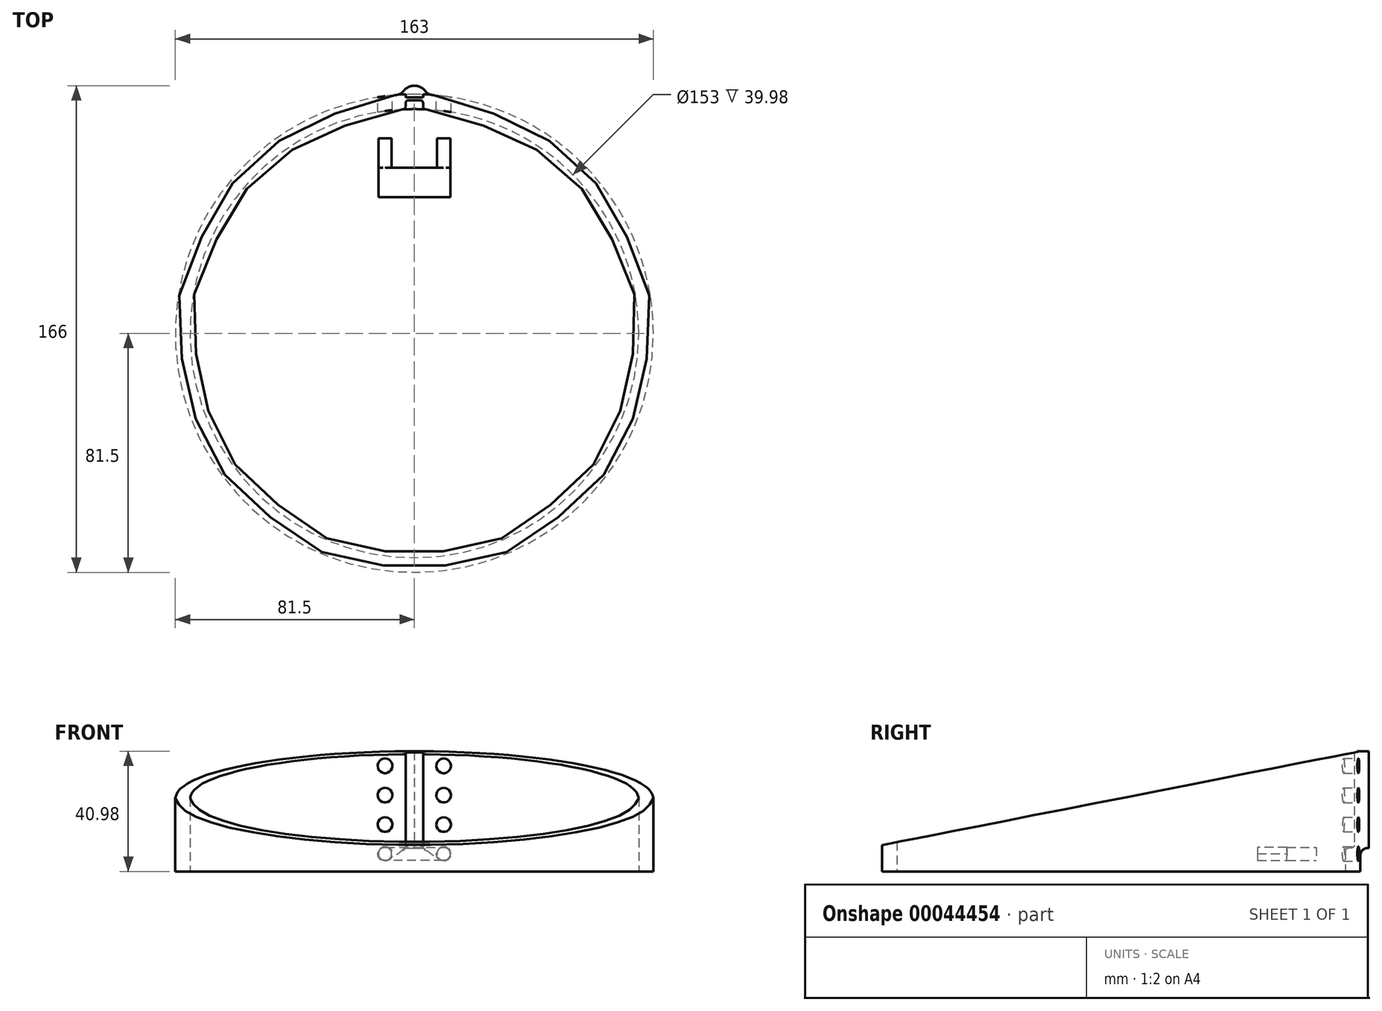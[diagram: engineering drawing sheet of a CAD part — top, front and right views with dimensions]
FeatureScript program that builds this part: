
annotation { "Feature Type Name" : "Feature", "Feature Type Description" : "" }
export const myFeature = defineFeature(function(context is Context, id is Id, definition is map)
    precondition{}
    {
        {
            var Q0;
            Q0=qCreatedBy(makeId("Top.planeOp"),FACE);
            var sketch = newSketch(context, id + "F0", { "sketchPlane" : qUnion([Q0])});
            skCircle(sketch, "E0", {"center": v(0, 0) * mm, "radius": 76.5 * mm});
            skCircle(sketch, "E1.0", {"center": v(0, 0) * mm, "radius": 81.5 * mm});
            skSolve(sketch);
        }
        {
            var Q0;
            Q0=qCreatedBy(makeId("Right.planeOp"),FACE);
            var sketch = newSketch(context, id + "F1", { "sketchPlane" : qUnion([Q0])});
            skLineSegment(sketch, "E2.0.0", {"start": v(-76.5, 0) * mm, "end": v(76.5, 0) * mm});
            skLineSegment(sketch, "E3", {"start": v(-76.5, 0) * mm, "end": v(-76.5, 10) * mm});
            skLineSegment(sketch, "E4", {"start": v(76.5, 0) * mm, "end": v(76.5, 40) * mm});
            skSolve(sketch);
        }
        {
            var Q0;
            Q0=sQuery(id+"F1.wireOp",VERTEX,"E3.end");
            var Q1;
            Q1=qCreatedBy(makeId("Front.planeOp"),FACE);
            cPlane(context, id + "F2", {"entities" : qUnion([Q0, Q1]), "cplaneType" : CPlaneType.PLANE_POINT, "offset" : 150 * mm, "width" : 150 * mm, "height" : 150 * mm});
        }
        {
            var Q0;
            Q0=qCreatedBy(id+"F2.planeOp",FACE);
            var sketch = newSketch(context, id + "F3", { "sketchPlane" : qUnion([Q0])});
            skLineSegment(sketch, "E5", {"start": v(0, 10) * mm, "end": v(-21.8, 10) * mm});
            skSolve(sketch);
        }
        {
            var Q0;
            Q0=sQuery(id+"F3.wireOp",EDGE,"E5");
            var Q1;
            Q1=sQuery(id+"F1.wireOp",VERTEX,"E4.end");
            cPlane(context, id + "F4", {"entities" : qUnion([Q0, Q1]), "cplaneType" : CPlaneType.LINE_ANGLE, "offset" : 150 * mm, "angle" : 0 * degree, "width" : 150 * mm, "height" : 150 * mm});
        }
        {
            var Q0;
            Q0=sQuery(id+"F1.wireOp",VERTEX,"E4.end");
            var Q1;
            Q1=qCreatedBy(makeId("Top.planeOp"),FACE);
            cPlane(context, id + "F5", {"entities" : qUnion([Q0, Q1]), "cplaneType" : CPlaneType.PLANE_POINT, "offset" : 150 * mm, "width" : 150 * mm, "height" : 150 * mm});
        }
        {
            var Q0;
            Q0=makeQuery(id+"F0.imprint","IMPRINT",FACE,{"disambiguationData":[TD([[makeQuery(id+"F0.imprint","IMPRINT",EDGE,{"derivedFrom":sQuery(id+"F0.wireOp",EDGE,"E0")}),-1.0]])]});
            var Q1;
            Q1=sQuery(id+"F0.wireOp",EDGE,"E1.0");
            var Q2;
            Q2=qCreatedBy(id+"F4.planeOp",FACE);
            extrude(context, id + "F6", {"entities" : qUnion([Q0]), "surfaceEntities" : qUnion([Q1]), "endBound" : BoundingType.UP_TO_SURFACE, "endBoundEntityFace" : qUnion([Q2]), "depth" : 19.21 * mm});
        }
        {
            var Q0;
            Q0=makeQuery(id+"F6.opExtrude","CAP_FACE",FACE,{"disambiguationData":[OSD([sQuery(id+"F0.wireOp",EDGE,"E0"),sQuery(id+"F0.wireOp",EDGE,"E1.0")])],"isStart":false});
            var sketch = newSketch(context, id + "F7", { "sketchPlane" : qUnion([Q0])});
            skLineSegment(sketch, "E6", {"start": v(-35.1, 87.86) * mm, "end": v(35.1, 87.86) * mm});
            skPoint(sketch, "E6.startSnap0", {"position": v(0, 87.86) * mm});
            skSolve(sketch);
        }
        {
            var Q0;
            Q0=sQuery(id+"F7.wireOp",EDGE,"E6");
            var Q1;
            Q1=qCreatedBy(makeId("Front.planeOp"),FACE);
            cPlane(context, id + "F8", {"entities" : qUnion([Q0, Q1]), "cplaneType" : CPlaneType.LINE_ANGLE, "offset" : 150 * mm, "angle" : 0 * degree, "width" : 150 * mm, "height" : 150 * mm});
        }
        {
            var Q0;
            Q0=qCreatedBy(id+"F8.planeOp",FACE);
            var sketch = newSketch(context, id + "F9", { "sketchPlane" : qUnion([Q0])});
            skLineSegment(sketch, "E7.0", {"start": v(35.1, 40.98) * mm, "end": v(-35.1, 40.98) * mm});
            skCircle(sketch, "E8", {"center": v(10, 36) * mm, "radius": 2.5 * mm});
            skCircle(sketch, "E9.0.1.0", {"center": v(-10, 36) * mm, "radius": 2.5 * mm});
            skCircle(sketch, "E9.1.0.0", {"center": v(10, 26) * mm, "radius": 2.5 * mm});
            skCircle(sketch, "E9.1.1.0", {"center": v(-10, 26) * mm, "radius": 2.5 * mm});
            skCircle(sketch, "E9.2.0.0", {"center": v(10, 16) * mm, "radius": 2.5 * mm});
            skCircle(sketch, "E9.2.1.0", {"center": v(-10, 16) * mm, "radius": 2.5 * mm});
            skLineSegment(sketch, "E9.direction1", {"start": v(10, 36) * mm, "end": v(10, 26) * mm, "construction": true});
            skLineSegment(sketch, "E9.direction2", {"start": v(10, 36) * mm, "end": v(-10, 36) * mm, "construction": true});
            skCircle(sketch, "E10.0.3.0", {"center": v(10, 6) * mm, "radius": 2.5 * mm});
            skCircle(sketch, "E10.0.3.1", {"center": v(-10, 6) * mm, "radius": 2.5 * mm});
            skSolve(sketch);
        }
        {
            var Q0;
            Q0=makeQuery(id+"F9.imprint","IMPRINT",FACE,{"disambiguationData":[TD([[makeQuery(id+"F9.imprint","IMPRINT",EDGE,{"derivedFrom":sQuery(id+"F9.wireOp",EDGE,"E9.0.1.0")}),1.0]])]});
            var Q1;
            Q1=makeQuery(id+"F9.imprint","IMPRINT",FACE,{"disambiguationData":[TD([[makeQuery(id+"F9.imprint","IMPRINT",EDGE,{"derivedFrom":sQuery(id+"F9.wireOp",EDGE,"E8")}),1.0]])]});
            var Q2;
            Q2=makeQuery(id+"F9.imprint","IMPRINT",FACE,{"disambiguationData":[TD([[makeQuery(id+"F9.imprint","IMPRINT",EDGE,{"derivedFrom":sQuery(id+"F9.wireOp",EDGE,"E9.1.0.0")}),1.0]])]});
            var Q3;
            Q3=makeQuery(id+"F9.imprint","IMPRINT",FACE,{"disambiguationData":[TD([[makeQuery(id+"F9.imprint","IMPRINT",EDGE,{"derivedFrom":sQuery(id+"F9.wireOp",EDGE,"E9.1.1.0")}),1.0]])]});
            var Q4;
            Q4=makeQuery(id+"F9.imprint","IMPRINT",FACE,{"disambiguationData":[TD([[makeQuery(id+"F9.imprint","IMPRINT",EDGE,{"derivedFrom":sQuery(id+"F9.wireOp",EDGE,"E9.2.1.0")}),1.0]])]});
            var Q5;
            Q5=makeQuery(id+"F9.imprint","IMPRINT",FACE,{"disambiguationData":[TD([[makeQuery(id+"F9.imprint","IMPRINT",EDGE,{"derivedFrom":sQuery(id+"F9.wireOp",EDGE,"E9.2.0.0")}),1.0]])]});
            var Q6;
            Q6=makeQuery(id+"F9.imprint","IMPRINT",FACE,{"disambiguationData":[TD([[makeQuery(id+"F9.imprint","IMPRINT",EDGE,{"derivedFrom":sQuery(id+"F9.wireOp",EDGE,"E10.0.3.0")}),1.0]])]});
            var Q7;
            Q7=makeQuery(id+"F9.imprint","IMPRINT",FACE,{"disambiguationData":[TD([[makeQuery(id+"F9.imprint","IMPRINT",EDGE,{"derivedFrom":sQuery(id+"F9.wireOp",EDGE,"E10.0.3.1")}),1.0]])]});
            var Q8;
            Q8=sQuery(id+"F9.wireOp",EDGE,"E8");
            var Q9;
            Q9=sQuery(id+"F9.wireOp",EDGE,"E9.0.1.0");
            var Q10;
            Q10=sQuery(id+"F9.wireOp",EDGE,"E9.1.1.0");
            var Q11;
            Q11=sQuery(id+"F9.wireOp",EDGE,"E9.1.0.0");
            var Q12;
            Q12=sQuery(id+"F9.wireOp",EDGE,"E9.2.0.0");
            var Q13;
            Q13=sQuery(id+"F9.wireOp",EDGE,"E10.0.3.0");
            var Q14;
            Q14=sQuery(id+"F9.wireOp",EDGE,"E10.0.3.1");
            var Q15;
            Q15=sQuery(id+"F9.wireOp",EDGE,"E9.2.1.0");
            var Q16;
            Q16=makeQuery(id+"F6.opExtrude","SWEPT_FACE",FACE,{"disambiguationData":[OSD([sQuery(id+"F0.wireOp",EDGE,"E0")])]});
            extrude(context, id + "F10", {"entities" : qUnion([Q0, Q1, Q2, Q3, Q4, Q5, Q6, Q7]), "operationType" : NewBodyOperationType.REMOVE, "surfaceEntities" : qUnion([Q8, Q9, Q10, Q11, Q12, Q13, Q14, Q15]), "endBound" : BoundingType.UP_TO_SURFACE, "oppositeDirection" : true, "endBoundEntityFace" : qUnion([Q16]), "depth" : 25 * mm});
        }
        {
            var Q0;
            Q0=qCreatedBy(id+"F8.planeOp",FACE);
            cPlane(context, id + "F11", {"entities" : qUnion([Q0]), "cplaneType" : CPlaneType.OFFSET, "offset" : 15 * mm, "oppositeDirection" : true, "width" : 150 * mm, "height" : 150 * mm});
        }
        {
            var Q0;
            Q0=qCreatedBy(id+"F11.planeOp",FACE);
            var sketch = newSketch(context, id + "F12", { "sketchPlane" : qUnion([Q0])});
            skCircle(sketch, "E11.0", {"center": v(10, 6) * mm, "radius": 2.5 * mm});
            skCircle(sketch, "E12.0", {"center": v(-10, 6) * mm, "radius": 2.5 * mm});
            skCircle(sketch, "E13.0", {"center": v(10, 6) * mm, "radius": 2.25 * mm});
            skCircle(sketch, "E14.0", {"center": v(-10, 6) * mm, "radius": 2.25 * mm});
            skSolve(sketch);
        }
        {
            var Q0;
            Q0=makeQuery(id+"F12.imprint","IMPRINT",FACE,{"disambiguationData":[TD([[makeQuery(id+"F12.imprint","IMPRINT",EDGE,{"derivedFrom":sQuery(id+"F12.wireOp",EDGE,"E13.0")}),1.0]])]});
            var Q1;
            Q1=makeQuery(id+"F12.imprint","IMPRINT",FACE,{"disambiguationData":[TD([[makeQuery(id+"F12.imprint","IMPRINT",EDGE,{"derivedFrom":sQuery(id+"F12.wireOp",EDGE,"E14.0")}),1.0]])]});
            var Q2;
            Q2=sQuery(id+"F12.wireOp",EDGE,"E13.0");
            var Q3;
            Q3=sQuery(id+"F12.wireOp",EDGE,"E14.0");
            extrude(context, id + "F13", {"entities" : qUnion([Q0, Q1]), "surfaceEntities" : qUnion([Q2, Q3]), "oppositeDirection" : true, "depth" : 10 * mm});
        }
        {
            var Q0;
            Q0=makeQuery(id+"F13.opExtrude","CAP_FACE",FACE,{"disambiguationData":[OSD([sQuery(id+"F12.wireOp",EDGE,"E13.0")])],"isStart":false});
            cPlane(context, id + "F14", {"entities" : qUnion([Q0]), "cplaneType" : CPlaneType.OFFSET, "offset" : 0 * mm, "width" : 150 * mm, "height" : 150 * mm});
        }
        {
            var Q0;
            Q0=qCreatedBy(id+"F14.planeOp",FACE);
            var sketch = newSketch(context, id + "F15", { "sketchPlane" : qUnion([Q0])});
            skPoint(sketch, "E15", {"position": v(0, 8.25) * mm});
            skCircle(sketch, "E16.0", {"center": v(-10, 6) * mm, "radius": 2.25 * mm});
            skCircle(sketch, "E17.0", {"center": v(10, 6) * mm, "radius": 2.25 * mm});
            skLineSegment(sketch, "E18", {"start": v(-12.25, 8.25) * mm, "end": v(12.25, 8.25) * mm});
            skLineSegment(sketch, "E19", {"start": v(12.25, 8.25) * mm, "end": v(12.25, 3.75) * mm});
            skLineSegment(sketch, "E20", {"start": v(12.25, 3.75) * mm, "end": v(-12.25, 3.75) * mm});
            skLineSegment(sketch, "E21", {"start": v(-12.25, 3.75) * mm, "end": v(-12.25, 8.25) * mm});
            skSolve(sketch);
        }
        {
            var Q0;
            {var subQ0=sQuery(id+"F15.wireOp",EDGE,"E21");var subQ1=sQuery(id+"F15.wireOp",EDGE,"E16.0");var subQ2=makeQuery(id+"F15.imprint","INTERSECT",VERTEX,{"derivedFrom":[subQ1,subQ0]});Q0=makeQuery(id+"F15.imprint","IMPRINT",FACE,{"disambiguationData":[TD([[makeQuery(id+"F15.imprint","IMPRINT",EDGE,{"disambiguationData":[TD([[subQ2,-1.0]])],"derivedFrom":subQ1}),-1.0]])]});}
            var Q1;
            {var subQ1=sQuery(id+"F15.wireOp",EDGE,"E16.0");var subQ3=sQuery(id+"F15.wireOp",EDGE,"E21");var subQ5=makeQuery(id+"F15.imprint","INTERSECT",VERTEX,{"derivedFrom":[subQ1,subQ3]});Q1=makeQuery(id+"F15.imprint","IMPRINT",FACE,{"disambiguationData":[TD([[makeQuery(id+"F15.imprint","IMPRINT",EDGE,{"disambiguationData":[TD([[subQ5,1.0]])],"derivedFrom":subQ1}),-1.0]])]});}
            var Q2;
            {var subQ0=sQuery(id+"F15.wireOp",EDGE,"E16.0");var subQ3=makeQuery(id+"F15.imprint","INTERSECT",VERTEX,{"derivedFrom":[subQ0,sQuery(id+"F15.wireOp",EDGE,"E21")]});Q2=makeQuery(id+"F15.imprint","IMPRINT",FACE,{"disambiguationData":[TD([[makeQuery(id+"F15.imprint","IMPRINT",EDGE,{"disambiguationData":[TD([[subQ3,1.0]])],"derivedFrom":subQ0}),1.0]])]});}
            var Q3;
            {var subQ0=sQuery(id+"F15.wireOp",EDGE,"E18");var subQ3=sQuery(id+"F15.wireOp",EDGE,"E16.0");var subQ4=makeQuery(id+"F15.imprint","INTERSECT",VERTEX,{"derivedFrom":[subQ3,subQ0]});Q3=makeQuery(id+"F15.imprint","IMPRINT",FACE,{"disambiguationData":[TD([[makeQuery(id+"F15.imprint","IMPRINT",EDGE,{"disambiguationData":[TD([[subQ4,1.0]])],"derivedFrom":subQ3}),-1.0]])]});}
            var Q4;
            {var subQ1=sQuery(id+"F15.wireOp",EDGE,"E17.0");var subQ3=sQuery(id+"F15.wireOp",EDGE,"E18");var subQ5=makeQuery(id+"F15.imprint","INTERSECT",VERTEX,{"derivedFrom":[subQ1,subQ3]});Q4=makeQuery(id+"F15.imprint","IMPRINT",FACE,{"disambiguationData":[TD([[makeQuery(id+"F15.imprint","IMPRINT",EDGE,{"disambiguationData":[TD([[subQ5,1.0]])],"derivedFrom":subQ1}),-1.0]])]});}
            var Q5;
            {var subQ1=sQuery(id+"F15.wireOp",EDGE,"E17.0");var subQ3=sQuery(id+"F15.wireOp",EDGE,"E19");var subQ5=makeQuery(id+"F15.imprint","INTERSECT",VERTEX,{"derivedFrom":[subQ1,subQ3]});Q5=makeQuery(id+"F15.imprint","IMPRINT",FACE,{"disambiguationData":[TD([[makeQuery(id+"F15.imprint","IMPRINT",EDGE,{"disambiguationData":[TD([[subQ5,1.0]])],"derivedFrom":subQ1}),-1.0]])]});}
            var Q6;
            {var subQ0=sQuery(id+"F15.wireOp",EDGE,"E17.0");var subQ3=makeQuery(id+"F15.imprint","INTERSECT",VERTEX,{"derivedFrom":[subQ0,sQuery(id+"F15.wireOp",EDGE,"E18")]});Q6=makeQuery(id+"F15.imprint","IMPRINT",FACE,{"disambiguationData":[TD([[makeQuery(id+"F15.imprint","IMPRINT",EDGE,{"disambiguationData":[TD([[subQ3,1.0]])],"derivedFrom":subQ0}),1.0]])]});}
            extrude(context, id + "F16", {"entities" : qUnion([Q0, Q1, Q2, Q3, Q4, Q5, Q6]), "operationType" : NewBodyOperationType.ADD, "depth" : 10 * mm});
        }
        {
            var Q0;
            Q0=makeQuery(id+"F16.opExtrude","SWEPT_EDGE",EDGE,{"disambiguationData":[OSD([sQuery(id+"F15.wireOp",EDGE,"a8bffe18-86e8-4c1c-b8b7-40149721dabd.bottom"),sQuery(id+"F15.wireOp",EDGE,"a8bffe18-86e8-4c1c-b8b7-40149721dabd.right")])]});
            var Q1;
            Q1=makeQuery(id+"F16.opExtrude","SWEPT_EDGE",EDGE,{"disambiguationData":[OSD([sQuery(id+"F15.wireOp",EDGE,"a8bffe18-86e8-4c1c-b8b7-40149721dabd.bottom"),sQuery(id+"F15.wireOp",EDGE,"a8bffe18-86e8-4c1c-b8b7-40149721dabd.left")])]});
            var Q2;
            Q2=makeQuery(id+"F16.opExtrude","CAP_EDGE",EDGE,{"disambiguationData":[OSD([sQuery(id+"F15.wireOp",EDGE,"a8bffe18-86e8-4c1c-b8b7-40149721dabd.top")])],"isStart":false});
            var Q3;
            Q3=makeQuery(id+"F16.opExtrude","CAP_EDGE",EDGE,{"disambiguationData":[OSD([sQuery(id+"F15.wireOp",EDGE,"a8bffe18-86e8-4c1c-b8b7-40149721dabd.top")])],"isStart":true});
            var Q4;
            Q4=makeQuery(id+"F16.opExtrude","SWEPT_EDGE",EDGE,{"disambiguationData":[OSD([sQuery(id+"F15.wireOp",EDGE,"E18"),sQuery(id+"F15.wireOp",EDGE,"E21")])]});
            var Q5;
            Q5=makeQuery(id+"F16.opExtrude","SWEPT_EDGE",EDGE,{"disambiguationData":[OSD([sQuery(id+"F15.wireOp",EDGE,"E20"),sQuery(id+"F15.wireOp",EDGE,"E21")])]});
            var Q6;
            Q6=makeQuery(id+"F16.opExtrude","SWEPT_EDGE",EDGE,{"disambiguationData":[OSD([sQuery(id+"F15.wireOp",EDGE,"E18"),sQuery(id+"F15.wireOp",EDGE,"E19")])]});
            var Q7;
            Q7=makeQuery(id+"F16.opExtrude","SWEPT_EDGE",EDGE,{"disambiguationData":[OSD([sQuery(id+"F15.wireOp",EDGE,"E19"),sQuery(id+"F15.wireOp",EDGE,"E20")])]});
            fillet(context, id + "F17", {"entities" : qUnion([Q0, Q1, Q2, Q3, Q4, Q5, Q6, Q7]), "radius" : 2.5 * mm, "tangentPropagation" : true, "rho" : 0.5, "crossSection" : FilletCrossSection.CONIC, "allowEdgeOverflow" : false});
        }
        {
            var Q0;
            Q0=qCreatedBy(id+"F8.planeOp",FACE);
            cPlane(context, id + "F18", {"entities" : qUnion([Q0]), "cplaneType" : CPlaneType.OFFSET, "offset" : 6 * mm, "oppositeDirection" : true, "width" : 150 * mm, "height" : 150 * mm});
        }
        {
            var Q0;
            Q0=qCreatedBy(id+"F8.planeOp",FACE);
            cPlane(context, id + "F19", {"entities" : qUnion([Q0]), "cplaneType" : CPlaneType.OFFSET, "offset" : 1 * mm, "oppositeDirection" : true, "width" : 150 * mm, "height" : 150 * mm});
        }
        {
            var Q0;
            Q0=qCreatedBy(id+"F19.planeOp",FACE);
            var sketch = newSketch(context, id + "F20", { "sketchPlane" : qUnion([Q0])});
            skLineSegment(sketch, "E22.0", {"start": v(0, 0) * mm, "end": v(0, 40) * mm});
            skLineSegment(sketch, "E23.bottom", {"start": v(3, 8) * mm, "end": v(-3, 8) * mm});
            skLineSegment(sketch, "E23.top", {"start": v(3, 40.98) * mm, "end": v(-3, 40.98) * mm});
            skLineSegment(sketch, "E23.left", {"start": v(3, 8) * mm, "end": v(3, 40.98) * mm});
            skLineSegment(sketch, "E23.right", {"start": v(-3, 8) * mm, "end": v(-3, 40.98) * mm});
            skPoint(sketch, "E24", {"position": v(0, 8) * mm});
            skSolve(sketch);
        }
        {
            var Q0;
            Q0=makeQuery(id+"F20.imprint","IMPRINT",FACE,{"disambiguationData":[TD([[makeQuery(id+"F20.imprint","IMPRINT",EDGE,{"derivedFrom":sQuery(id+"F20.wireOp",EDGE,"E23.top")}),1.0]])]});
            extrude(context, id + "F21", {"entities" : qUnion([Q0]), "operationType" : NewBodyOperationType.ADD, "depth" : 4 * mm});
        }
        {
            var Q0;
            Q0=qCreatedBy(id+"F18.planeOp",FACE);
            var sketch = newSketch(context, id + "F22", { "sketchPlane" : qUnion([Q0])});
            skLineSegment(sketch, "E25.0", {"start": v(3, 8) * mm, "end": v(-3, 8) * mm});
            skLineSegment(sketch, "E26", {"start": v(3, 8) * mm, "end": v(3, 44.14) * mm});
            skLineSegment(sketch, "E27", {"start": v(3, 44.14) * mm, "end": v(-3, 44.14) * mm});
            skLineSegment(sketch, "E28", {"start": v(-3, 44.14) * mm, "end": v(-3, 8) * mm});
            skSolve(sketch);
        }
        {
            var Q0;
            Q0=makeQuery(id+"F22.imprint","IMPRINT",FACE,{"disambiguationData":[TD([[makeQuery(id+"F22.imprint","IMPRINT",EDGE,{"derivedFrom":sQuery(id+"F22.wireOp",EDGE,"E25.0")}),-1.0]])]});
            extrude(context, id + "F23", {"entities" : qUnion([Q0]), "operationType" : NewBodyOperationType.REMOVE, "depth" : 4 * mm});
        }
        {
            var Q0;
            Q0=makeQuery(id+"F23.boolean.opBoolean","COPY",EDGE,{"derivedFrom":makeQuery(id+"F23.opExtrude","CAP_EDGE",EDGE,{"disambiguationData":[OSD([sQuery(id+"F22.wireOp",EDGE,"E26")])],"isStart":false})});
            var Q1;
            Q1=makeQuery(id+"F23.boolean.opBoolean","INTERSECT",EDGE,{"derivedFrom":[makeQuery(id+"F6.opExtrude","SWEPT_FACE",FACE,{"disambiguationData":[OSD([sQuery(id+"F0.wireOp",EDGE,"E0")])]}),makeQuery(id+"F23.opExtrude","SWEPT_FACE",FACE,{"disambiguationData":[OSD([sQuery(id+"F22.wireOp",EDGE,"E26")])]})]});
            var Q2;
            Q2=makeQuery(id+"F23.boolean.opBoolean","COPY",EDGE,{"derivedFrom":makeQuery(id+"F23.opExtrude","CAP_EDGE",EDGE,{"disambiguationData":[OSD([sQuery(id+"F22.wireOp",EDGE,"E28")])],"isStart":false})});
            var Q3;
            Q3=makeQuery(id+"F23.boolean.opBoolean","INTERSECT",EDGE,{"derivedFrom":[makeQuery(id+"F6.opExtrude","SWEPT_FACE",FACE,{"disambiguationData":[OSD([sQuery(id+"F0.wireOp",EDGE,"E0")])]}),makeQuery(id+"F23.opExtrude","SWEPT_FACE",FACE,{"disambiguationData":[OSD([sQuery(id+"F22.wireOp",EDGE,"E28")])]})]});
            var Q4;
            Q4=makeQuery(id+"F23.boolean.opBoolean","INTERSECT",EDGE,{"derivedFrom":[makeQuery(id+"F6.opExtrude","SWEPT_FACE",FACE,{"disambiguationData":[OSD([sQuery(id+"F0.wireOp",EDGE,"E0")])]}),makeQuery(id+"F23.opExtrude","SWEPT_FACE",FACE,{"disambiguationData":[OSD([sQuery(id+"F22.wireOp",EDGE,"E25.0")])]})]});
            var Q5;
            Q5=makeQuery(id+"F23.boolean.opBoolean","COPY",EDGE,{"derivedFrom":makeQuery(id+"F23.opExtrude","CAP_EDGE",EDGE,{"disambiguationData":[OSD([sQuery(id+"F22.wireOp",EDGE,"E25.0")])],"isStart":false})});
            fillet(context, id + "F24", {"entities" : qUnion([Q0, Q1, Q2, Q3, Q4, Q5]), "radius" : 1 * mm, "tangentPropagation" : true, "allowEdgeOverflow" : false});
        }
        {
            var Q0;
            Q0=makeQuery(id+"F21.boolean.opBoolean","INTERSECT",EDGE,{"derivedFrom":[makeQuery(id+"F6.opExtrude","SWEPT_FACE",FACE,{"disambiguationData":[OSD([sQuery(id+"F0.wireOp",EDGE,"E1.0")])]}),makeQuery(id+"F21.opExtrude","SWEPT_FACE",FACE,{"disambiguationData":[OSD([sQuery(id+"F20.wireOp",EDGE,"E23.left")])]})]});
            var Q1;
            Q1=makeQuery(id+"F21.boolean.opBoolean","INTERSECT",EDGE,{"derivedFrom":[makeQuery(id+"F6.opExtrude","SWEPT_FACE",FACE,{"disambiguationData":[OSD([sQuery(id+"F0.wireOp",EDGE,"E1.0")])]}),makeQuery(id+"F21.opExtrude","SWEPT_FACE",FACE,{"disambiguationData":[OSD([sQuery(id+"F20.wireOp",EDGE,"E23.right")])]})]});
            fillet(context, id + "F25", {"entities" : qUnion([Q0, Q1]), "radius" : 4 * mm, "tangentPropagation" : true, "rho" : 0.5, "crossSection" : FilletCrossSection.CONIC, "allowEdgeOverflow" : false});
        }
        {
            var Q0;
            {var subQ0=sQuery(id+"F20.wireOp",EDGE,"E23.right");Q0=makeQuery(id+"F25.opFillet","BLEND_EDGE",EDGE,{"blendedFrom":[makeQuery(id+"F21.boolean.opBoolean","INTERSECT",EDGE,{"derivedFrom":[makeQuery(id+"F6.opExtrude","SWEPT_FACE",FACE,{"disambiguationData":[OSD([sQuery(id+"F0.wireOp",EDGE,"E1.0")])]}),makeQuery(id+"F21.opExtrude","SWEPT_FACE",FACE,{"disambiguationData":[OSD([subQ0])]})]}),makeQuery(id+"F21.opExtrude","CAP_FACE",FACE,{"disambiguationData":[OSD([sQuery(id+"F20.wireOp",EDGE,"E23.bottom"),sQuery(id+"F20.wireOp",EDGE,"E23.top"),sQuery(id+"F20.wireOp",EDGE,"E23.left"),subQ0])],"isStart":false})],"blendedInto":[makeQuery(id+"F21.opExtrude","CAP_FACE",FACE,{"disambiguationData":[OSD([sQuery(id+"F20.wireOp",EDGE,"E23.bottom"),sQuery(id+"F20.wireOp",EDGE,"E23.top"),sQuery(id+"F20.wireOp",EDGE,"E23.left"),subQ0])],"isStart":false})]});}
            var Q1;
            {var subQ0=sQuery(id+"F20.wireOp",EDGE,"E23.left");Q1=makeQuery(id+"F25.opFillet","BLEND_EDGE",EDGE,{"blendedFrom":[makeQuery(id+"F21.boolean.opBoolean","INTERSECT",EDGE,{"derivedFrom":[makeQuery(id+"F6.opExtrude","SWEPT_FACE",FACE,{"disambiguationData":[OSD([sQuery(id+"F0.wireOp",EDGE,"E1.0")])]}),makeQuery(id+"F21.opExtrude","SWEPT_FACE",FACE,{"disambiguationData":[OSD([subQ0])]})]}),makeQuery(id+"F21.opExtrude","CAP_FACE",FACE,{"disambiguationData":[OSD([sQuery(id+"F20.wireOp",EDGE,"E23.bottom"),sQuery(id+"F20.wireOp",EDGE,"E23.top"),subQ0,sQuery(id+"F20.wireOp",EDGE,"E23.right")])],"isStart":false})],"blendedInto":[makeQuery(id+"F21.opExtrude","CAP_FACE",FACE,{"disambiguationData":[OSD([sQuery(id+"F20.wireOp",EDGE,"E23.bottom"),sQuery(id+"F20.wireOp",EDGE,"E23.top"),subQ0,sQuery(id+"F20.wireOp",EDGE,"E23.right")])],"isStart":false})]});}
            fillet(context, id + "F26", {"entities" : qUnion([Q0, Q1]), "radius" : 5 * mm, "tangentPropagation" : true, "allowEdgeOverflow" : false});
        }
        {
            var Q0;
            Q0=makeQuery(id+"F21.boolean.opBoolean","INTERSECT",EDGE,{"derivedFrom":[makeQuery(id+"F6.opExtrude","SWEPT_FACE",FACE,{"disambiguationData":[OSD([sQuery(id+"F0.wireOp",EDGE,"E1.0")])]}),makeQuery(id+"F21.opExtrude","SWEPT_FACE",FACE,{"disambiguationData":[OSD([sQuery(id+"F20.wireOp",EDGE,"E23.bottom")])]})]});
            fillet(context, id + "F27", {"entities" : qUnion([Q0]), "radius" : 2.7 * mm, "tangentPropagation" : true, "allowEdgeOverflow" : false});
        }
    });
